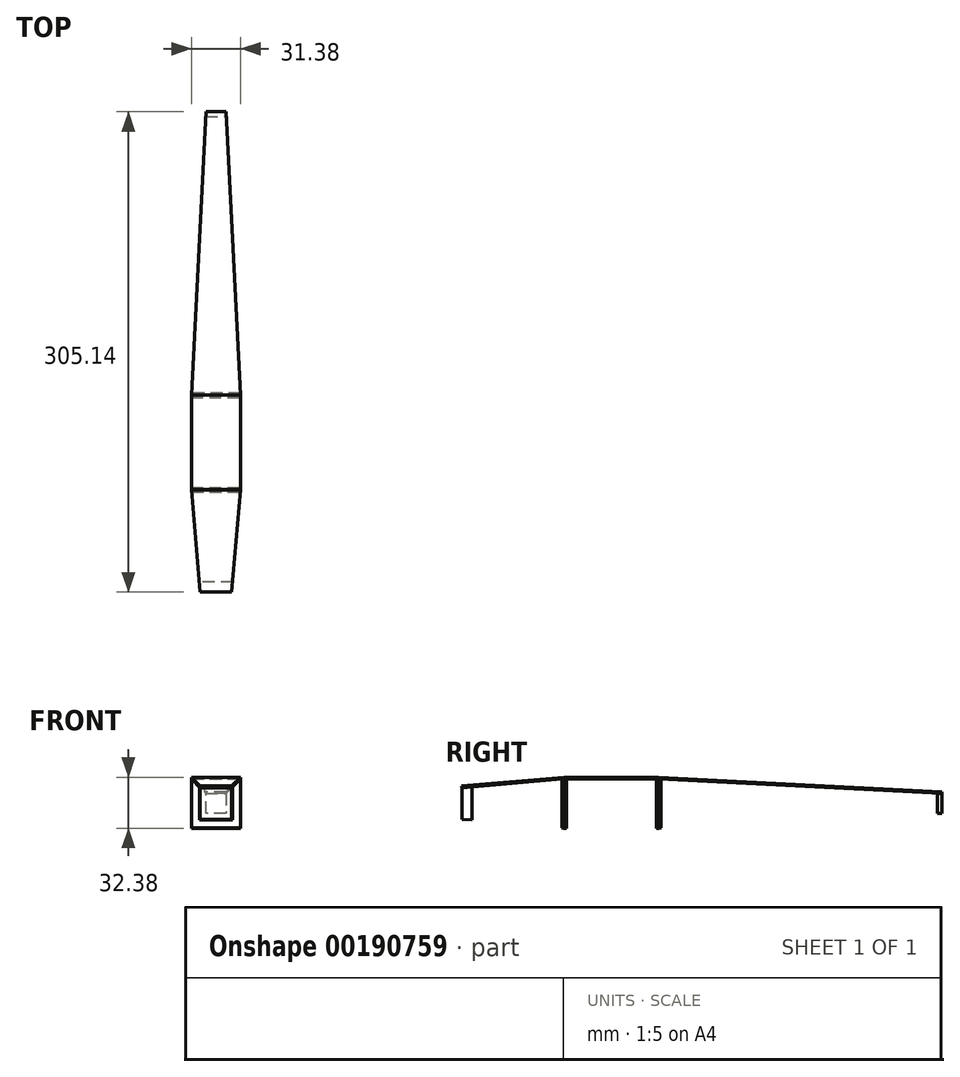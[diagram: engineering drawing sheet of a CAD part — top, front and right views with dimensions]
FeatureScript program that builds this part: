
annotation { "Feature Type Name" : "Feature", "Feature Type Description" : "" }
export const myFeature = defineFeature(function(context is Context, id is Id, definition is map)
    precondition{}
    {
        {
            var Q0;
            Q0=qCreatedBy(makeId("Front.planeOp"),FACE);
            var sketch = newSketch(context, id + "F0", { "sketchPlane" : qUnion([Q0])});
            skLineSegment(sketch, "E0.bottom", {"start": v(10, 10) * mm, "end": v(-10, 10) * mm});
            skLineSegment(sketch, "E0.top", {"start": v(10, -10) * mm, "end": v(-10, -10) * mm});
            skLineSegment(sketch, "E0.left", {"start": v(10, 10) * mm, "end": v(10, -10) * mm});
            skLineSegment(sketch, "E0.right", {"start": v(-10, 10) * mm, "end": v(-10, -10) * mm});
            skPoint(sketch, "E0.middle", {"position": v(0, 0) * mm});
            skSolve(sketch);
        }
        {
            var Q0;
            Q0 = qSketchRegion(id + "F0", true);
            extrude(context, id + "F1", {"entities" : qUnion([Q0]), "oppositeDirection" : true, "depth" : 6.5 * mm, "hasDraft" : true, "draftAngle" : 5 * degree});
        }
        {
            var Q0;
            Q0=qCreatedBy(makeId("Front.planeOp"),FACE);
            cPlane(context, id + "F2", {"entities" : qUnion([Q0]), "cplaneType" : CPlaneType.OFFSET, "offset" : 65 * mm, "oppositeDirection" : true, "width" : 150 * mm, "height" : 150 * mm});
        }
        {
            var Q0;
            Q0=makeQuery(id+"F1.opExtrude","SWEPT_FACE",FACE,{"disambiguationData":[OSD([sQuery(id+"F0.wireOp",EDGE,"E0.bottom")])]});
            var sketch = newSketch(context, id + "F3", { "sketchPlane" : qUnion([Q0])});
            skLineSegment(sketch, "E1.0", {"start": v(-15.69, 66.12) * mm, "end": v(-10, 0.87) * mm});
            skLineSegment(sketch, "E1.1", {"start": v(15.69, 66.12) * mm, "end": v(10, 0.87) * mm});
            skLineSegment(sketch, "E1.2", {"start": v(10, 0.87) * mm, "end": v(-10, 0.87) * mm});
            skPoint(sketch, "E2.orphan", {"position": v(-10.57, 7.4) * mm});
            skPoint(sketch, "E3.orphan", {"position": v(10.57, 7.4) * mm});
            skLineSegment(sketch, "E4", {"start": v(-15.69, 66.12) * mm, "end": v(15.69, 66.12) * mm});
            skSolve(sketch);
        }
        {
            var Q0;
            Q0 = qSketchRegion(id + "F3", true);
            extrude(context, id + "F4", {"entities" : qUnion([Q0]), "depth" : 1 * mm});
        }
        {
            var Q0;
            Q0=qCreatedBy(id+"F2.planeOp",FACE);
            var sketch = newSketch(context, id + "F5", { "sketchPlane" : qUnion([Q0])});
            skLineSegment(sketch, "E5.bottom", {"start": v(-15.69, 15.69) * mm, "end": v(15.69, 15.69) * mm});
            skLineSegment(sketch, "E5.top", {"start": v(-15.69, -15.69) * mm, "end": v(15.69, -15.69) * mm});
            skLineSegment(sketch, "E5.left", {"start": v(-15.69, 15.69) * mm, "end": v(-15.69, -15.69) * mm});
            skLineSegment(sketch, "E5.right", {"start": v(15.69, 15.69) * mm, "end": v(15.69, -15.69) * mm});
            skPoint(sketch, "E5.middle", {"position": v(0, 0) * mm});
            skSolve(sketch);
        }
        {
            var Q0;
            Q0=makeQuery(id+"F5.imprint","IMPRINT",FACE,{"disambiguationData":[TD([[makeQuery(id+"F5.imprint","IMPRINT",EDGE,{"derivedFrom":sQuery(id+"F5.wireOp",EDGE,"E5.bottom")}),-1.0]])]});
            extrude(context, id + "F6", {"entities" : qUnion([Q0]), "oppositeDirection" : true, "depth" : 1.5 * mm});
        }
        {
            var Q0;
            Q0=makeQuery(id+"F6.opExtrude","CAP_FACE",FACE,{"disambiguationData":[OSD([sQuery(id+"F5.wireOp",EDGE,"E5.bottom"),sQuery(id+"F5.wireOp",EDGE,"E5.top"),sQuery(id+"F5.wireOp",EDGE,"E5.left"),sQuery(id+"F5.wireOp",EDGE,"E5.right")])],"isStart":true});
            extrude(context, id + "F7", {"entities" : qUnion([Q0]), "operationType" : NewBodyOperationType.ADD, "depth" : 1.5 * mm, "hasDraft" : true, "draftAngle" : 5 * degree, "draftPullDirection" : true});
        }
        {
            var Q0;
            Q0=qCreatedBy(id+"F2.planeOp",FACE);
            cPlane(context, id + "F8", {"entities" : qUnion([Q0]), "cplaneType" : CPlaneType.OFFSET, "offset" : 60 * mm, "oppositeDirection" : true, "width" : 150 * mm, "height" : 150 * mm});
        }
        {
            var Q0;
            Q0=makeQuery(id+"F6.opExtrude","SWEPT_FACE",FACE,{"disambiguationData":[OSD([sQuery(id+"F5.wireOp",EDGE,"E5.bottom")])]});
            var sketch = newSketch(context, id + "F9", { "sketchPlane" : qUnion([Q0])});
            skLineSegment(sketch, "E6.bottom", {"start": v(15.69, 65) * mm, "end": v(-15.69, 65) * mm});
            skLineSegment(sketch, "E6.top", {"start": v(15.69, 125) * mm, "end": v(-15.69, 125) * mm});
            skLineSegment(sketch, "E6.left", {"start": v(15.69, 65) * mm, "end": v(15.69, 125) * mm});
            skLineSegment(sketch, "E6.right", {"start": v(-15.69, 65) * mm, "end": v(-15.69, 125) * mm});
            skSolve(sketch);
        }
        {
            var Q0;
            Q0 = qSketchRegion(id + "F9", true);
            extrude(context, id + "F10", {"entities" : qUnion([Q0]), "depth" : 1 * mm});
        }
        {
            var Q0;
            Q0=qCreatedBy(id+"F8.planeOp",FACE);
            var sketch = newSketch(context, id + "F11", { "sketchPlane" : qUnion([Q0])});
            skLineSegment(sketch, "E7.bottom", {"start": v(-15.69, 15.69) * mm, "end": v(15.69, 15.69) * mm});
            skLineSegment(sketch, "E7.top", {"start": v(-15.69, -15.69) * mm, "end": v(15.69, -15.69) * mm});
            skLineSegment(sketch, "E7.left", {"start": v(-15.69, 15.69) * mm, "end": v(-15.69, -15.69) * mm});
            skLineSegment(sketch, "E7.right", {"start": v(15.69, 15.69) * mm, "end": v(15.69, -15.69) * mm});
            skPoint(sketch, "E7.middle", {"position": v(0, 0) * mm});
            skSolve(sketch);
        }
        {
            var Q0;
            Q0 = qSketchRegion(id + "F11", true);
            extrude(context, id + "F12", {"entities" : qUnion([Q0]), "depth" : 1.5 * mm});
        }
        {
            var Q0;
            Q0=makeQuery(id+"F12.opExtrude","CAP_FACE",FACE,{"disambiguationData":[OSD([sQuery(id+"F11.wireOp",EDGE,"E7.bottom"),sQuery(id+"F11.wireOp",EDGE,"E7.top"),sQuery(id+"F11.wireOp",EDGE,"E7.left"),sQuery(id+"F11.wireOp",EDGE,"E7.right")])],"isStart":true});
            extrude(context, id + "F13", {"entities" : qUnion([Q0]), "operationType" : NewBodyOperationType.ADD, "depth" : 1.5 * mm, "hasDraft" : true, "draftAngle" : 3 * degree, "draftPullDirection" : true});
        }
        {
            var Q0;
            Q0=qCreatedBy(id+"F8.planeOp",FACE);
            cPlane(context, id + "F14", {"entities" : qUnion([Q0]), "cplaneType" : CPlaneType.OFFSET, "offset" : 180 * mm, "oppositeDirection" : true, "width" : 150 * mm, "height" : 150 * mm});
        }
        {
            var Q0;
            Q0=makeQuery(id+"F13.opExtrude","SWEPT_FACE",FACE,{"disambiguationData":[OSD([sQuery(id+"F11.wireOp",EDGE,"E7.bottom")])]});
            var sketch = newSketch(context, id + "F15", { "sketchPlane" : qUnion([Q0])});
            skLineSegment(sketch, "E8.bottom", {"start": v(15.69, 124) * mm, "end": v(-15.69, 124) * mm});
            skLineSegment(sketch, "E8.top", {"start": v(6.25, 304.25) * mm, "end": v(-6.25, 304.25) * mm});
            skLineSegment(sketch, "E8.left", {"start": v(15.69, 124) * mm, "end": v(6.25, 304.25) * mm});
            skLineSegment(sketch, "E8.right", {"start": v(-15.69, 124) * mm, "end": v(-6.25, 304.25) * mm});
            skPoint(sketch, "E9", {"position": v(0, 304.25) * mm});
            skLineSegment(sketch, "E10", {"start": v(0, 304.25) * mm, "end": v(0, 125.5) * mm, "construction": true});
            skSolve(sketch);
        }
        {
            var Q0;
            Q0 = qSketchRegion(id + "F15", true);
            extrude(context, id + "F16", {"entities" : qUnion([Q0]), "depth" : 1 * mm});
        }
        {
            var Q0;
            Q0=qCreatedBy(id+"F14.planeOp",FACE);
            var sketch = newSketch(context, id + "F17", { "sketchPlane" : qUnion([Q0])});
            skLineSegment(sketch, "E11.bottom", {"start": v(6.25, 6.25) * mm, "end": v(-6.25, 6.25) * mm});
            skLineSegment(sketch, "E11.top", {"start": v(6.25, -6.25) * mm, "end": v(-6.25, -6.25) * mm});
            skLineSegment(sketch, "E11.left", {"start": v(6.25, 6.25) * mm, "end": v(6.25, -6.25) * mm});
            skLineSegment(sketch, "E11.right", {"start": v(-6.25, 6.25) * mm, "end": v(-6.25, -6.25) * mm});
            skPoint(sketch, "E11.middle", {"position": v(0, 0) * mm});
            skSolve(sketch);
        }
        {
            var Q0;
            Q0 = qSketchRegion(id + "F17", true);
            extrude(context, id + "F18", {"entities" : qUnion([Q0]), "depth" : 3 * mm, "hasDraft" : true, "draftAngle" : 3 * degree});
        }
    });
